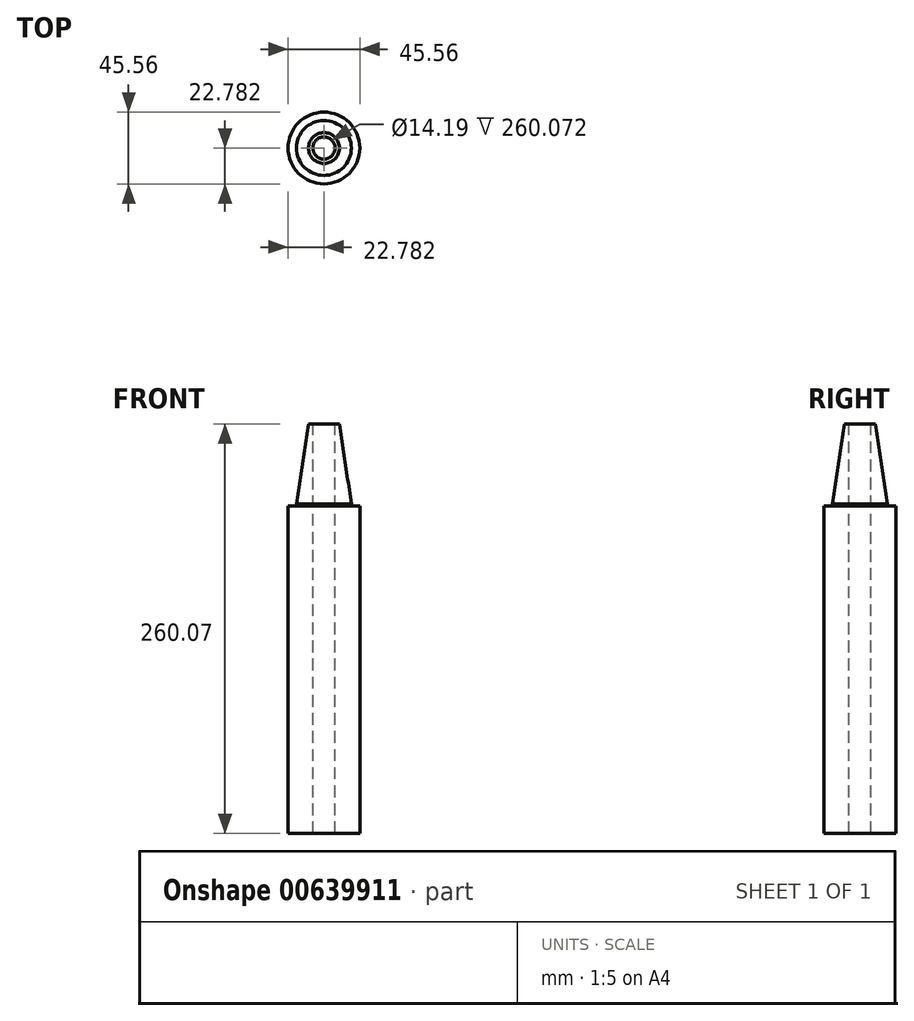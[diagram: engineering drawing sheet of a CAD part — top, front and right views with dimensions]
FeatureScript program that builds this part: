
annotation { "Feature Type Name" : "Feature", "Feature Type Description" : "" }
export const myFeature = defineFeature(function(context is Context, id is Id, definition is map)
    precondition{}
    {
        {
            var Q0;
            Q0=qCreatedBy(makeId("Top.planeOp"),FACE);
            var sketch = newSketch(context, id + "F0", { "sketchPlane" : qUnion([Q0])});
            skCircle(sketch, "E0", {"center": v(18.94, 20.04) * mm, "radius": 22.78 * mm});
            skSolve(sketch);
        }
        {
            var Q0;
            Q0=makeQuery(id+"F0.imprint","IMPRINT",FACE,{"disambiguationData":[TD([[makeQuery(id+"F0.imprint","IMPRINT",EDGE,{"derivedFrom":sQuery(id+"F0.wireOp",EDGE,"E0")}),1.0]])]});
            extrude(context, id + "F1", {"entities" : qUnion([Q0]), "depth" : 207.9 * mm, "offsetDistance" : 25.4 * mm});
        }
        {
            var Q0;
            Q0=makeQuery(id+"F1.opExtrude","CAP_FACE",FACE,{"disambiguationData":[OSD([sQuery(id+"F0.wireOp",EDGE,"E0")])],"isStart":false});
            var sketch = newSketch(context, id + "F2", { "sketchPlane" : qUnion([Q0])});
            skCircle(sketch, "E1", {"center": v(18.94, 20.04) * mm, "radius": 17.43 * mm});
            skSolve(sketch);
        }
        {
            var Q0;
            Q0=makeQuery(id+"F2.imprint","IMPRINT",FACE,{"disambiguationData":[TD([[makeQuery(id+"F2.imprint","IMPRINT",EDGE,{"derivedFrom":sQuery(id+"F2.wireOp",EDGE,"E1")}),1.0]])]});
            extrude(context, id + "F3", {"entities" : qUnion([Q0]), "operationType" : NewBodyOperationType.ADD, "depth" : 52.16 * mm, "offsetDistance" : 25.4 * mm});
        }
        {
            var Q0;
            Q0=makeQuery(id+"F3.opExtrude","CAP_EDGE",EDGE,{"disambiguationData":[OSD([sQuery(id+"F2.wireOp",EDGE,"E1")])],"isStart":false});
            chamfer(context, id + "F4", {"entities" : qUnion([Q0]), "chamferType" : ChamferType.TWO_OFFSETS, "width1" : 7.62 * mm, "oppositeDirection" : false, "width2" : 50.8 * mm, "tangentPropagation" : true});
        }
        {
            var Q0;
            Q0=makeQuery(id+"F3.opExtrude","CAP_FACE",FACE,{"disambiguationData":[OSD([sQuery(id+"F2.wireOp",EDGE,"E1")])],"isStart":false});
            var sketch = newSketch(context, id + "F5", { "sketchPlane" : qUnion([Q0])});
            skCircle(sketch, "E2", {"center": v(18.94, 20.04) * mm, "radius": 7.1 * mm});
            skSolve(sketch);
        }
        {
            var Q0;
            Q0=makeQuery(id+"F5.imprint","IMPRINT",FACE,{"disambiguationData":[TD([[makeQuery(id+"F5.imprint","IMPRINT",EDGE,{"derivedFrom":sQuery(id+"F5.wireOp",EDGE,"E2")}),1.0]])]});
            extrude(context, id + "F6", {"entities" : qUnion([Q0]), "operationType" : NewBodyOperationType.REMOVE, "oppositeDirection" : true, "depth" : 295.3 * mm, "offsetDistance" : 25.4 * mm});
        }
    });
